# Revit family: 221010023038804
name_source: partatom
category: Modelos genéricos
units: mm (PartAtom-declared; Revit-internal decimal feet)

## family parameters
Compartido = No
Corte con vacíos al cargar = No
Cota de conector redondo = Diámetro de uso
Puede alojar armadura = No
Punto de cálculo de habitación = No
Se basa en plano de trabajo = No
Siempre vertical = No
Tipo de pieza = Normal

## types (1)
- PERNO CLIP INICIO RAINBODECK ACERO INOX N2 NEGRO
    Aplicacion = Perno requerido para la instalación de las tablas de Deck de WPC
    Color = Negro
    Dimension = 0 mm  [stored 0 ft]
    Empresa = CNP SPA.
    Espesor = 0 mm  [stored 0 ft]
    Material = Acero inoxidable
    Modelo = PERNO CLIP INICIO RAINBODECK
    Nombre SKU = PERNO CLIP INICIO RAINBODECK ACERO INOX N2 NEGRO
    Num SKUs = 221010023038804
    URL = https://www.empresascnp.cl
    Unidad = Por unidad.
    Url Ficha tecnica = https://empresascnp.cl

note: [stored X ft] marks values corroborated as IEEE doubles in the binary element streams (Revit-internal decimal feet)

## geometry (parser evidence)
native form markers: Sweep x2
no freeform markers — native parametric forms only
